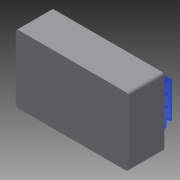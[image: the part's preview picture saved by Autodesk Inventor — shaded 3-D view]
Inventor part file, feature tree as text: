
AUTODESK INVENTOR PART (.ipt)
format: ipt  version: 2015 (Build 190159000, 159)  size: 186,880 bytes
history: native  units: mm
features: extrude x3, sketch x3, fillet x1, projected_geometry x1
ambient origin geometry x8: Origin, YZ Plane, XZ Plane, XY Plane, X Axis, Y Axis, Z Axis, Center Point
bodies: Solid1 (feature_tree)
feature tree (8):
  extrude  "Extrusion1"  Depth=120.0mm
  extrude  "Extrusion2"  Depth=3.5mm
  sketch  "Sketch3"  dims[d7=10.0mm d8=19.0mm d9=10.0mm d10=19.0mm d11=10.0mm d12=19.0mm d13=10.0mm d14=19.0mm d15=5.0mm d16=5.0mm d17=5.0mm d18=5.0mm d19=5.0mm d20=5.0mm d21=5.0mm d22=5.0mm d23=5.0mm d24=15.0mm d35=3.0mm d36=22.0mm d37=3.0mm d41=3.0mm d44=20.0mm d45=20.0mm d51=5.0mm d54=175.0mm d55=3.0mm d57=3.0mm d59=160.0mm d60=3.0mm d62=90.0mm d63=3.0mm d64=20.0mm d65=20.0mm d66=3.0mm d67=3.0mm d68=3.0mm d69=3.0mm d70=5.6mm d71=0.0mm d72=138.0mm d73=3.5mm d74=3.5mm d75=3.5mm d78=3.5mm]
  fillet  "Fillet2"  Radius=60.0mm
  extrude  "Extrusion4"  Depth=3.5mm
  sketch  "Sketch1"  dims[d0=200.0mm d1=120.0mm]
  sketch  "Sketch2"  dims[d2=3.0mm d3=0.0mm d4=3.5mm d5=60.0mm d6=0.0mm]
  projected_geometry  "Projected Loop1"
